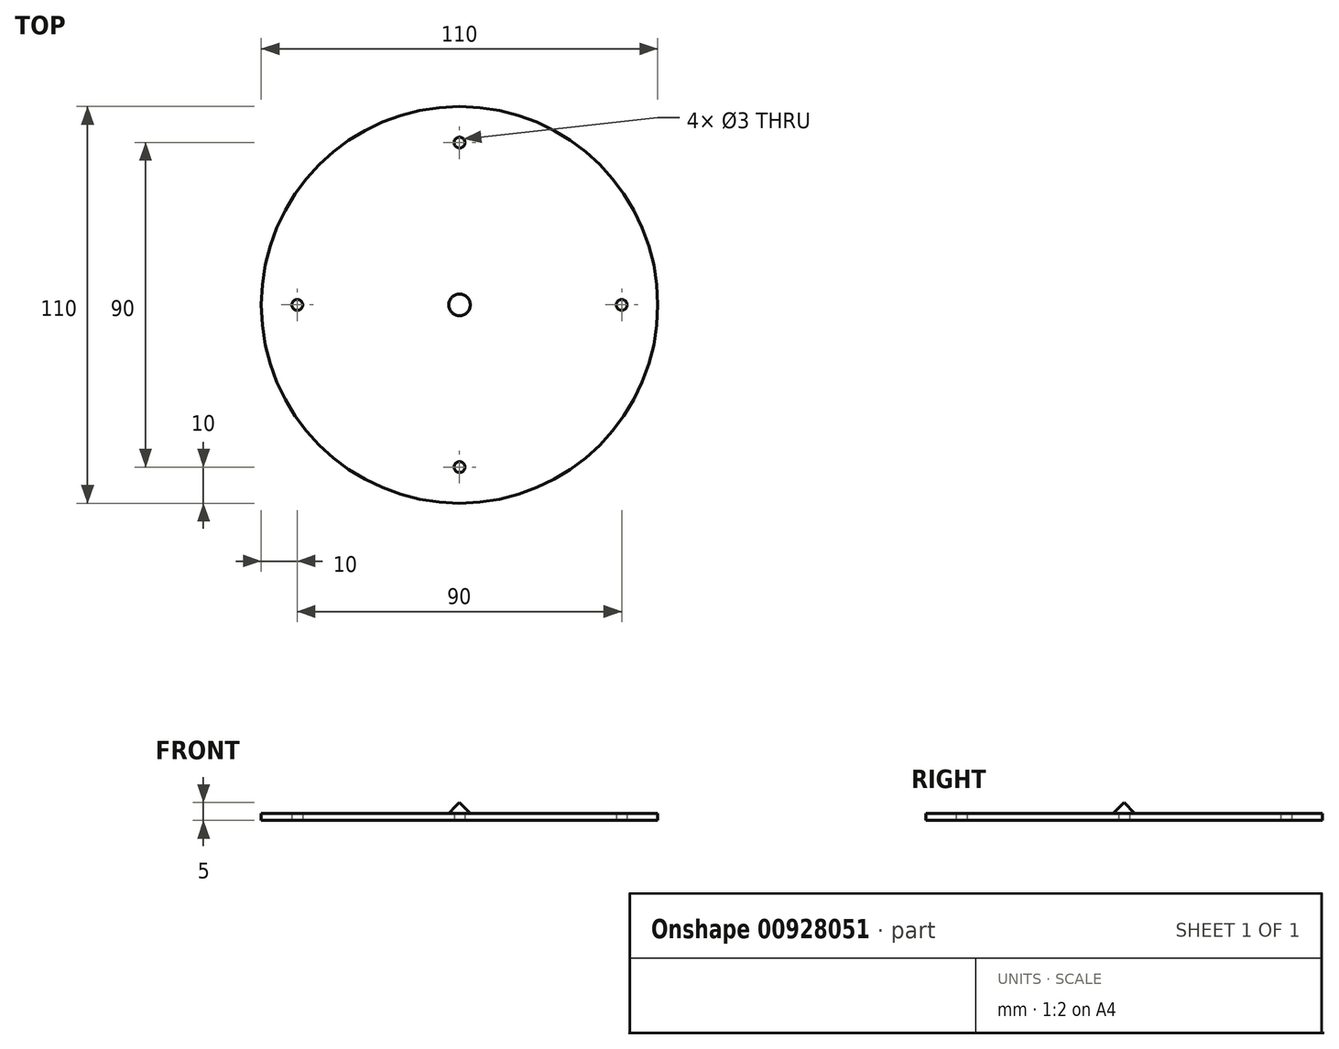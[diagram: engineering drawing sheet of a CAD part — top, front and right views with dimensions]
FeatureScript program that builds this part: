
annotation { "Feature Type Name" : "Feature", "Feature Type Description" : "" }
export const myFeature = defineFeature(function(context is Context, id is Id, definition is map)
    precondition{}
    {
        {
            var Q0;
            Q0=qCreatedBy(makeId("Top.planeOp"),FACE);
            var sketch = newSketch(context, id + "F0", { "sketchPlane" : qUnion([Q0])});
            skCircle(sketch, "E0", {"center": v(0, 0) * mm, "radius": 55 * mm});
            skSolve(sketch);
        }
        {
            var Q0;
            Q0=makeQuery(id+"F0.imprint","IMPRINT",FACE,{"disambiguationData":[TD([[makeQuery(id+"F0.imprint","IMPRINT",EDGE,{"derivedFrom":sQuery(id+"F0.wireOp",EDGE,"E0")}),1.0]])]});
            extrude(context, id + "F1", {"entities" : qUnion([Q0]), "depth" : 2 * mm, "offsetDistance" : 25 * mm});
        }
        {
            var Q0;
            Q0=makeQuery(id+"F1.opExtrude","CAP_FACE",FACE,{"disambiguationData":[OSD([sQuery(id+"F0.wireOp",EDGE,"E0")])],"isStart":true});
            var sketch = newSketch(context, id + "F2", { "sketchPlane" : qUnion([Q0])});
            skCircle(sketch, "E1", {"center": v(45, 0) * mm, "radius": 1.5 * mm});
            skCircle(sketch, "E2.1.0", {"center": v(0, 45) * mm, "radius": 1.5 * mm});
            skCircle(sketch, "E2.2.0", {"center": v(-45, 0) * mm, "radius": 1.5 * mm});
            skCircle(sketch, "E2.3.0", {"center": v(0, -45) * mm, "radius": 1.5 * mm});
            skPoint(sketch, "E2.center", {"position": v(0, 0) * mm});
            skSolve(sketch);
        }
        {
            var Q0;
            Q0=makeQuery(id+"F2.imprint","IMPRINT",FACE,{"disambiguationData":[TD([[makeQuery(id+"F2.imprint","IMPRINT",EDGE,{"derivedFrom":sQuery(id+"F2.wireOp",EDGE,"E2.2.0")}),1.0]])]});
            var Q1;
            Q1=makeQuery(id+"F2.imprint","IMPRINT",FACE,{"disambiguationData":[TD([[makeQuery(id+"F2.imprint","IMPRINT",EDGE,{"derivedFrom":sQuery(id+"F2.wireOp",EDGE,"E2.1.0")}),1.0]])]});
            var Q2;
            Q2=makeQuery(id+"F2.imprint","IMPRINT",FACE,{"disambiguationData":[TD([[makeQuery(id+"F2.imprint","IMPRINT",EDGE,{"derivedFrom":sQuery(id+"F2.wireOp",EDGE,"E1")}),1.0]])]});
            var Q3;
            Q3=makeQuery(id+"F2.imprint","IMPRINT",FACE,{"disambiguationData":[TD([[makeQuery(id+"F2.imprint","IMPRINT",EDGE,{"derivedFrom":sQuery(id+"F2.wireOp",EDGE,"E2.3.0")}),1.0]])]});
            extrude(context, id + "F3", {"entities" : qUnion([Q0, Q1, Q2, Q3]), "operationType" : NewBodyOperationType.REMOVE, "oppositeDirection" : true, "depth" : 25 * mm, "offsetDistance" : 25 * mm});
        }
        {
            var Q0;
            Q0=makeQuery(id+"F1.opExtrude","CAP_FACE",FACE,{"disambiguationData":[OSD([sQuery(id+"F0.wireOp",EDGE,"E0")])],"isStart":false});
            var sketch = newSketch(context, id + "F4", { "sketchPlane" : qUnion([Q0])});
            skCircle(sketch, "E3", {"center": v(0, 0) * mm, "radius": 5 * mm});
            skSolve(sketch);
        }
        {
            var Q0;
            Q0=makeQuery(id+"F4.imprint","IMPRINT",FACE,{"disambiguationData":[TD([[makeQuery(id+"F4.imprint","IMPRINT",EDGE,{"derivedFrom":sQuery(id+"F4.wireOp",EDGE,"E3")}),1.0]])]});
            extrude(context, id + "F5", {"entities" : qUnion([Q0]), "operationType" : NewBodyOperationType.ADD, "depth" : 3 * mm, "offsetDistance" : 25 * mm});
        }
        {
            var Q0;
            Q0=makeQuery(id+"F5.opExtrude","CAP_EDGE",EDGE,{"disambiguationData":[OSD([sQuery(id+"F4.wireOp",EDGE,"E3")])],"isStart":false});
            chamfer(context, id + "F6", {"entities" : qUnion([Q0]), "chamferType" : ChamferType.TWO_OFFSETS, "width1" : 5 * mm, "oppositeDirection" : false, "width2" : 5 * mm, "tangentPropagation" : true});
        }
    });
